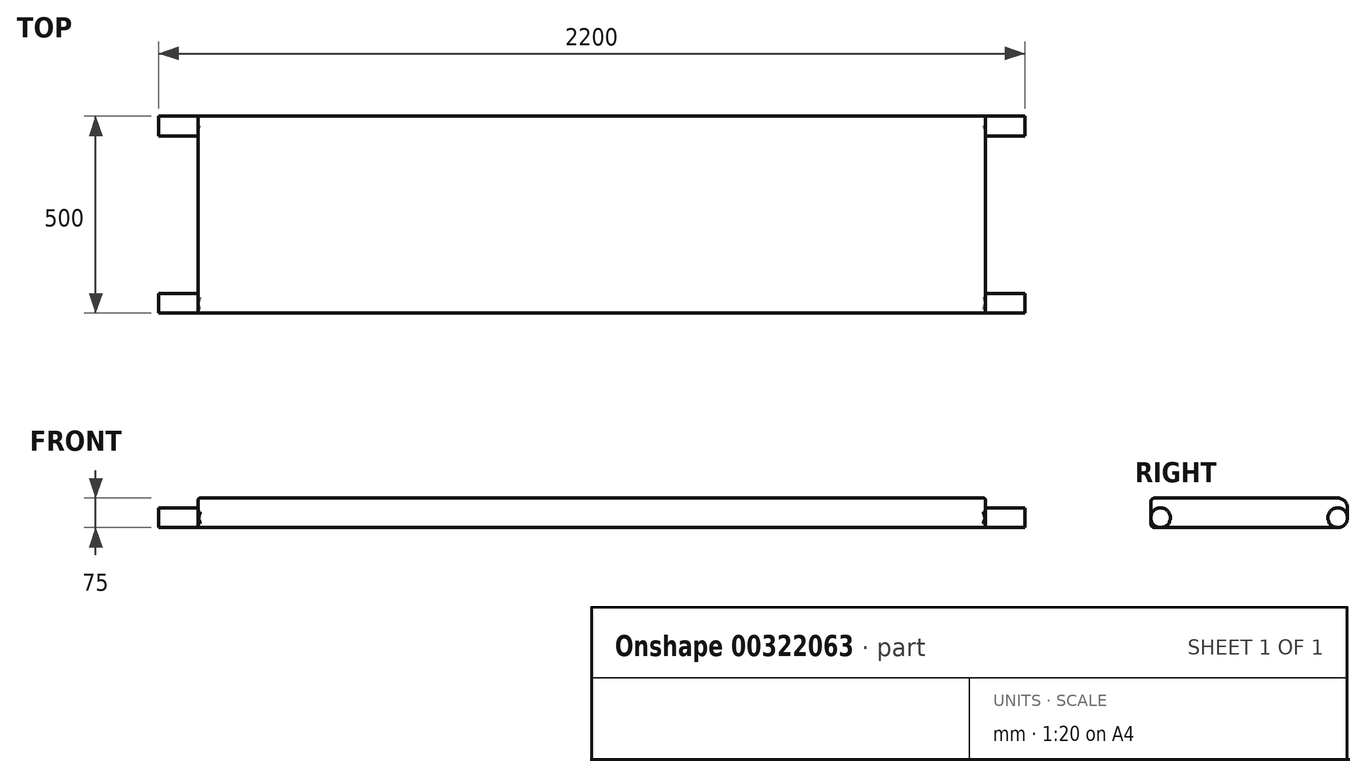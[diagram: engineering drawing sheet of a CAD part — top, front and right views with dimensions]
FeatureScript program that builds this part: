
annotation { "Feature Type Name" : "Feature", "Feature Type Description" : "" }
export const myFeature = defineFeature(function(context is Context, id is Id, definition is map)
    precondition{}
    {
        {
            var Q0;
            Q0=qCreatedBy(makeId("Top.planeOp"),FACE);
            var sketch = newSketch(context, id + "F0", { "sketchPlane" : qUnion([Q0])});
            skLineSegment(sketch, "E0.bottom", {"start": v(1000, -250) * mm, "end": v(-1000, -250) * mm});
            skLineSegment(sketch, "E0.top", {"start": v(1000, 250) * mm, "end": v(-1000, 250) * mm});
            skLineSegment(sketch, "E0.left", {"start": v(1000, -250) * mm, "end": v(1000, 250) * mm});
            skLineSegment(sketch, "E0.right", {"start": v(-1000, -250) * mm, "end": v(-1000, 250) * mm});
            skPoint(sketch, "E0.middle", {"position": v(0, 0) * mm});
            skSolve(sketch);
        }
        {
            var Q0;
            Q0=makeQuery(id+"F0.imprint","IMPRINT",FACE,{"disambiguationData":[TD([[makeQuery(id+"F0.imprint","IMPRINT",EDGE,{"derivedFrom":sQuery(id+"F0.wireOp",EDGE,"E0.bottom")}),-1.0]])]});
            var Q1;
            Q1=makeQuery(id+"F0.imprint","IMPRINT",FACE,{"disambiguationData":[TD([[makeQuery(id+"F0.imprint","IMPRINT",EDGE,{"derivedFrom":sQuery(id+"F0.wireOp",EDGE,"YRQeZQn4-7Cbb-9UCJ-M20K-rFLxlKPOlhtP.bottom")}),-1.0]])]});
            var Q2;
            Q2=makeQuery(id+"F0.imprint","IMPRINT",FACE,{"disambiguationData":[TD([[makeQuery(id+"F0.imprint","IMPRINT",EDGE,{"derivedFrom":sQuery(id+"F0.wireOp",EDGE,"G8XYoKp5-aqa8-jmf0-HJoe-nbpIYL89vVyW.bottom")}),1.0]])]});
            var Q3;
            Q3=makeQuery(id+"F0.imprint","IMPRINT",FACE,{"disambiguationData":[TD([[makeQuery(id+"F0.imprint","IMPRINT",EDGE,{"derivedFrom":sQuery(id+"F0.wireOp",EDGE,"YKcLL9iq-yqm1-ACdf-Vv9F-fHLMxW8R1gZK.bottom")}),1.0]])]});
            var Q4;
            Q4=makeQuery(id+"F0.imprint","IMPRINT",FACE,{"disambiguationData":[TD([[makeQuery(id+"F0.imprint","IMPRINT",EDGE,{"derivedFrom":sQuery(id+"F0.wireOp",EDGE,"gcKQsa7a-Bflu-mnZn-lMUR-VRSaT6CXQkLw.bottom")}),-1.0]])]});
            extrude(context, id + "F1", {"entities" : qUnion([Q0, Q1, Q2, Q3, Q4]), "depth" : 75 * mm});
        }
        {
            var Q0;
            Q0=makeQuery(id+"F1.opExtrude","SWEPT_FACE",FACE,{"disambiguationData":[OSD([sQuery(id+"F0.wireOp",EDGE,"E0.right")])]});
            var sketch = newSketch(context, id + "F2", { "sketchPlane" : qUnion([Q0])});
            skCircle(sketch, "E1", {"center": v(-225, 25) * mm, "radius": 25 * mm});
            skPoint(sketch, "E2.centerSnap0", {"position": v(250, 37.5) * mm});
            skCircle(sketch, "E3", {"center": v(225, 25) * mm, "radius": 25 * mm});
            skSolve(sketch);
        }
        {
            var Q0;
            Q0 = qSketchRegion(id + "F2", true);
            extrude(context, id + "F3", {"entities" : qUnion([Q0]), "operationType" : NewBodyOperationType.ADD, "depth" : 100 * mm});
        }
        {
            var Q0;
            Q0=makeQuery(id+"F1.opExtrude","SWEPT_FACE",FACE,{"disambiguationData":[OSD([sQuery(id+"F0.wireOp",EDGE,"E0.left")])]});
            var sketch = newSketch(context, id + "F4", { "sketchPlane" : qUnion([Q0])});
            skCircle(sketch, "E4", {"center": v(225, 25) * mm, "radius": 25 * mm});
            skPoint(sketch, "E5.centerSnap0", {"position": v(-250, 37.5) * mm});
            skCircle(sketch, "E6", {"center": v(-225, 25) * mm, "radius": 25 * mm});
            skSolve(sketch);
        }
        {
            var Q0;
            Q0 = qSketchRegion(id + "F4", true);
            extrude(context, id + "F5", {"entities" : qUnion([Q0]), "operationType" : NewBodyOperationType.ADD, "depth" : 100 * mm});
        }
        {
            var Q0;
            Q0=makeQuery(id+"F1.opExtrude","CAP_EDGE",EDGE,{"disambiguationData":[OSD([sQuery(id+"F0.wireOp",EDGE,"E0.top")])],"isStart":true});
            fillet(context, id + "F6", {"entities" : qUnion([Q0]), "radius" : 25 * mm, "tangentPropagation" : true, "allowEdgeOverflow" : false});
        }
        {
            var Q0;
            Q0=makeQuery(id+"F1.opExtrude","CAP_EDGE",EDGE,{"disambiguationData":[OSD([sQuery(id+"F0.wireOp",EDGE,"E0.top")])],"isStart":false});
            fillet(context, id + "F7", {"entities" : qUnion([Q0]), "radius" : 25 * mm, "tangentPropagation" : true, "allowEdgeOverflow" : false});
        }
        {
            var Q0;
            Q0=makeQuery(id+"F1.opExtrude","CAP_EDGE",EDGE,{"disambiguationData":[OSD([sQuery(id+"F0.wireOp",EDGE,"E0.left")])],"isStart":false});
            var Q1;
            {var subQ0=sQuery(id+"F0.wireOp",EDGE,"E0.left");Q1=makeQuery(id+"F5.boolean.opBoolean","SPLIT",EDGE,{"disambiguationData":[TD([makeQuery(id+"F1.opExtrude","CAP_FACE",FACE,{"disambiguationData":[OSD([sQuery(id+"F0.wireOp",EDGE,"E0.bottom"),sQuery(id+"F0.wireOp",EDGE,"E0.top"),subQ0,sQuery(id+"F0.wireOp",EDGE,"E0.right")])],"isStart":true}),makeQuery(id+"F1.opExtrude","SWEPT_FACE",FACE,{"disambiguationData":[OSD([subQ0])]}),makeQuery(id+"F5.opExtrude","SWEPT_FACE",FACE,{"disambiguationData":[OSD([sQuery(id+"F4.wireOp",EDGE,"E4")])]}),makeQuery(id+"F5.opExtrude","SWEPT_FACE",FACE,{"disambiguationData":[OSD([sQuery(id+"F4.wireOp",EDGE,"E6")])]})])],"derivedFrom":makeQuery(id+"F1.opExtrude","CAP_EDGE",EDGE,{"disambiguationData":[OSD([subQ0])],"isStart":true})});}
            var Q2;
            Q2=makeQuery(id+"F1.opExtrude","CAP_EDGE",EDGE,{"disambiguationData":[OSD([sQuery(id+"F0.wireOp",EDGE,"E0.right")])],"isStart":false});
            var Q3;
            {var subQ0=sQuery(id+"F0.wireOp",EDGE,"E0.right");Q3=makeQuery(id+"F3.boolean.opBoolean","SPLIT",EDGE,{"disambiguationData":[TD([makeQuery(id+"F1.opExtrude","CAP_FACE",FACE,{"disambiguationData":[OSD([sQuery(id+"F0.wireOp",EDGE,"E0.bottom"),sQuery(id+"F0.wireOp",EDGE,"E0.top"),sQuery(id+"F0.wireOp",EDGE,"E0.left"),subQ0])],"isStart":true}),makeQuery(id+"F1.opExtrude","SWEPT_FACE",FACE,{"disambiguationData":[OSD([subQ0])]}),makeQuery(id+"F3.opExtrude","SWEPT_FACE",FACE,{"disambiguationData":[OSD([sQuery(id+"F2.wireOp",EDGE,"E1")])]}),makeQuery(id+"F3.opExtrude","SWEPT_FACE",FACE,{"disambiguationData":[OSD([sQuery(id+"F2.wireOp",EDGE,"E3")])]})])],"derivedFrom":makeQuery(id+"F1.opExtrude","CAP_EDGE",EDGE,{"disambiguationData":[OSD([subQ0])],"isStart":true})});}
            var Q4;
            {var subQ0=sQuery(id+"F0.wireOp",EDGE,"E0.bottom");var subQ1=sQuery(id+"F0.wireOp",EDGE,"E0.right");Q4=makeQuery(id+"F3.boolean.opBoolean","SPLIT",EDGE,{"disambiguationData":[TD([makeQuery(id+"F1.opExtrude","CAP_FACE",FACE,{"disambiguationData":[OSD([subQ0,sQuery(id+"F0.wireOp",EDGE,"E0.top"),sQuery(id+"F0.wireOp",EDGE,"E0.left"),subQ1])],"isStart":false})])],"derivedFrom":makeQuery(id+"F1.opExtrude","SWEPT_EDGE",EDGE,{"disambiguationData":[OSD([subQ0,subQ1])]})});}
            var Q5;
            {var subQ0=sQuery(id+"F0.wireOp",EDGE,"E0.bottom");var subQ1=sQuery(id+"F0.wireOp",EDGE,"E0.right");Q5=makeQuery(id+"F3.boolean.opBoolean","SPLIT",EDGE,{"disambiguationData":[TD([makeQuery(id+"F1.opExtrude","CAP_FACE",FACE,{"disambiguationData":[OSD([subQ0,sQuery(id+"F0.wireOp",EDGE,"E0.top"),sQuery(id+"F0.wireOp",EDGE,"E0.left"),subQ1])],"isStart":true})])],"derivedFrom":makeQuery(id+"F1.opExtrude","SWEPT_EDGE",EDGE,{"disambiguationData":[OSD([subQ0,subQ1])]})});}
            var Q6;
            {var subQ0=sQuery(id+"F0.wireOp",EDGE,"E0.bottom");var subQ1=sQuery(id+"F0.wireOp",EDGE,"E0.left");Q6=makeQuery(id+"F5.boolean.opBoolean","SPLIT",EDGE,{"disambiguationData":[TD([makeQuery(id+"F1.opExtrude","CAP_FACE",FACE,{"disambiguationData":[OSD([subQ0,sQuery(id+"F0.wireOp",EDGE,"E0.top"),subQ1,sQuery(id+"F0.wireOp",EDGE,"E0.right")])],"isStart":true})])],"derivedFrom":makeQuery(id+"F1.opExtrude","SWEPT_EDGE",EDGE,{"disambiguationData":[OSD([subQ0,subQ1])]})});}
            var Q7;
            {var subQ0=sQuery(id+"F0.wireOp",EDGE,"E0.bottom");var subQ1=sQuery(id+"F0.wireOp",EDGE,"E0.left");Q7=makeQuery(id+"F5.boolean.opBoolean","SPLIT",EDGE,{"disambiguationData":[TD([makeQuery(id+"F1.opExtrude","CAP_FACE",FACE,{"disambiguationData":[OSD([subQ0,sQuery(id+"F0.wireOp",EDGE,"E0.top"),subQ1,sQuery(id+"F0.wireOp",EDGE,"E0.right")])],"isStart":false})])],"derivedFrom":makeQuery(id+"F1.opExtrude","SWEPT_EDGE",EDGE,{"disambiguationData":[OSD([subQ0,subQ1])]})});}
            fillet(context, id + "F8", {"entities" : qUnion([Q0, Q1, Q2, Q3, Q4, Q5, Q6, Q7]), "radius" : 5 * mm, "tangentPropagation" : true, "allowEdgeOverflow" : false});
        }
        {
            var Q0;
            Q0=makeQuery(id+"F1.opExtrude","CAP_EDGE",EDGE,{"disambiguationData":[OSD([sQuery(id+"F0.wireOp",EDGE,"E0.bottom")])],"isStart":false});
            var Q1;
            Q1=makeQuery(id+"F1.opExtrude","CAP_EDGE",EDGE,{"disambiguationData":[OSD([sQuery(id+"F0.wireOp",EDGE,"E0.bottom")])],"isStart":true});
            fillet(context, id + "F9", {"entities" : qUnion([Q0, Q1]), "radius" : 10 * mm, "tangentPropagation" : true, "allowEdgeOverflow" : false});
        }
    });
